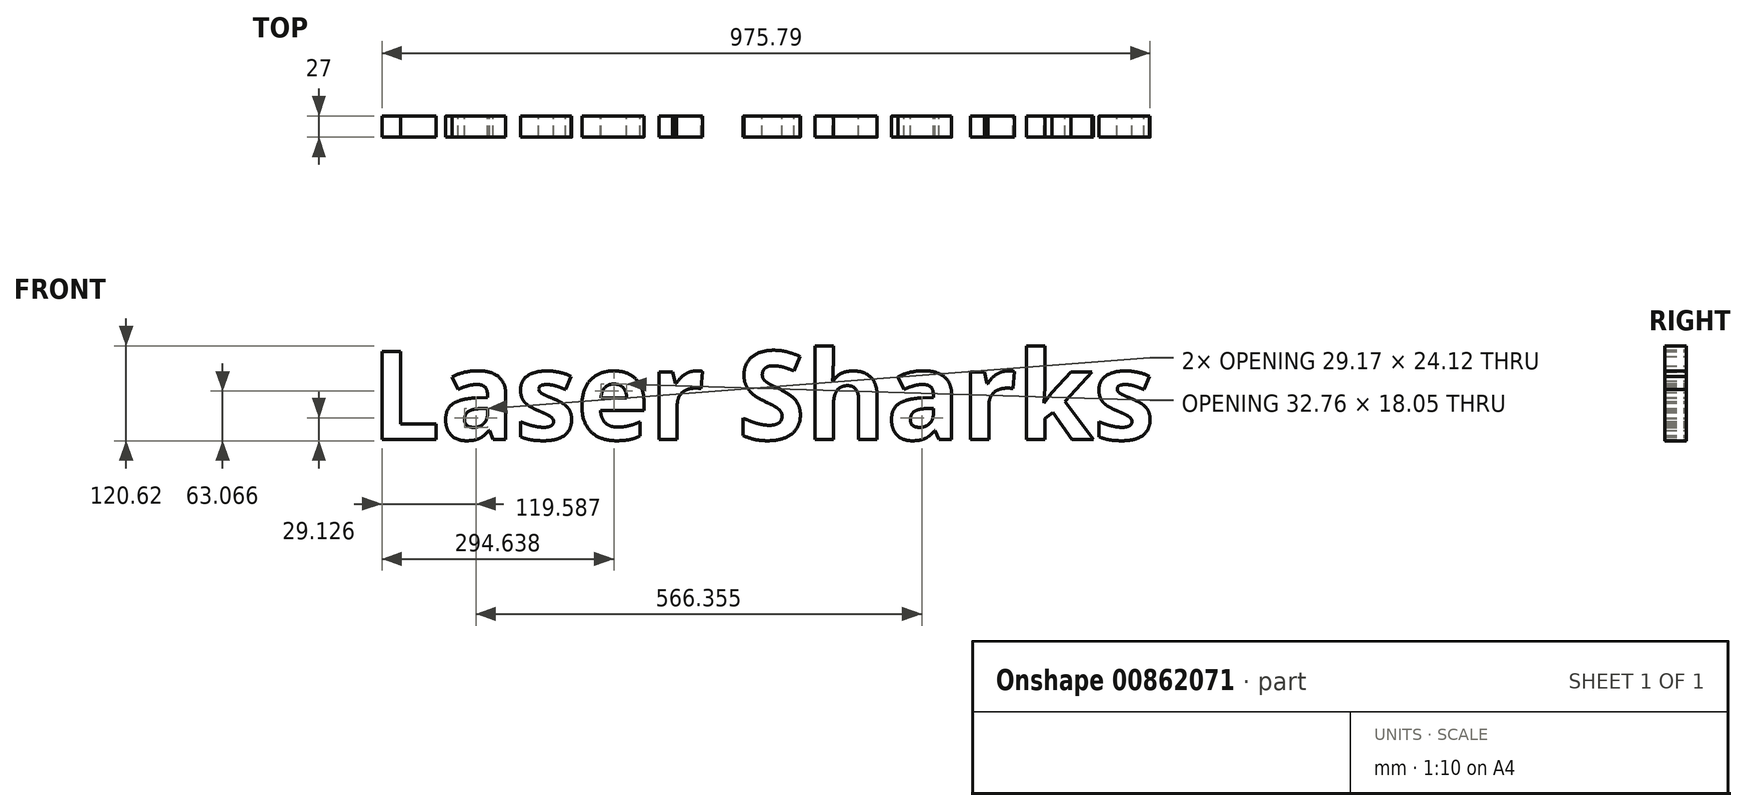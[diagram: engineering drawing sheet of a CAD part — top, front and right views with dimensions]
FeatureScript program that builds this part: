
annotation { "Feature Type Name" : "Feature", "Feature Type Description" : "" }
export const myFeature = defineFeature(function(context is Context, id is Id, definition is map)
    precondition{}
    {
        {
            var Q0;
            Q0=qCreatedBy(makeId("Front.planeOp"),FACE);
            var sketch = newSketch(context, id + "F0", { "sketchPlane" : qUnion([Q0])});
            skText(sketch, "E0", { "text": "Laser Sharks", "fontName": "OpenSans-Bold.ttf"});
            const initialGuessF0  = {"E0": [-0.50064, -0.05167, 1, 0, 0.11284]};
            skSetInitialGuess(sketch, initialGuessF0);
            skSolve(sketch);
        }
        {
            var Q0;
            Q0 = qSketchRegion(id + "F0", true);
            extrude(context, id + "F1", {"entities" : qUnion([Q0]), "depth" : 27 * mm, "offsetDistance" : 25 * mm});
        }
    });
